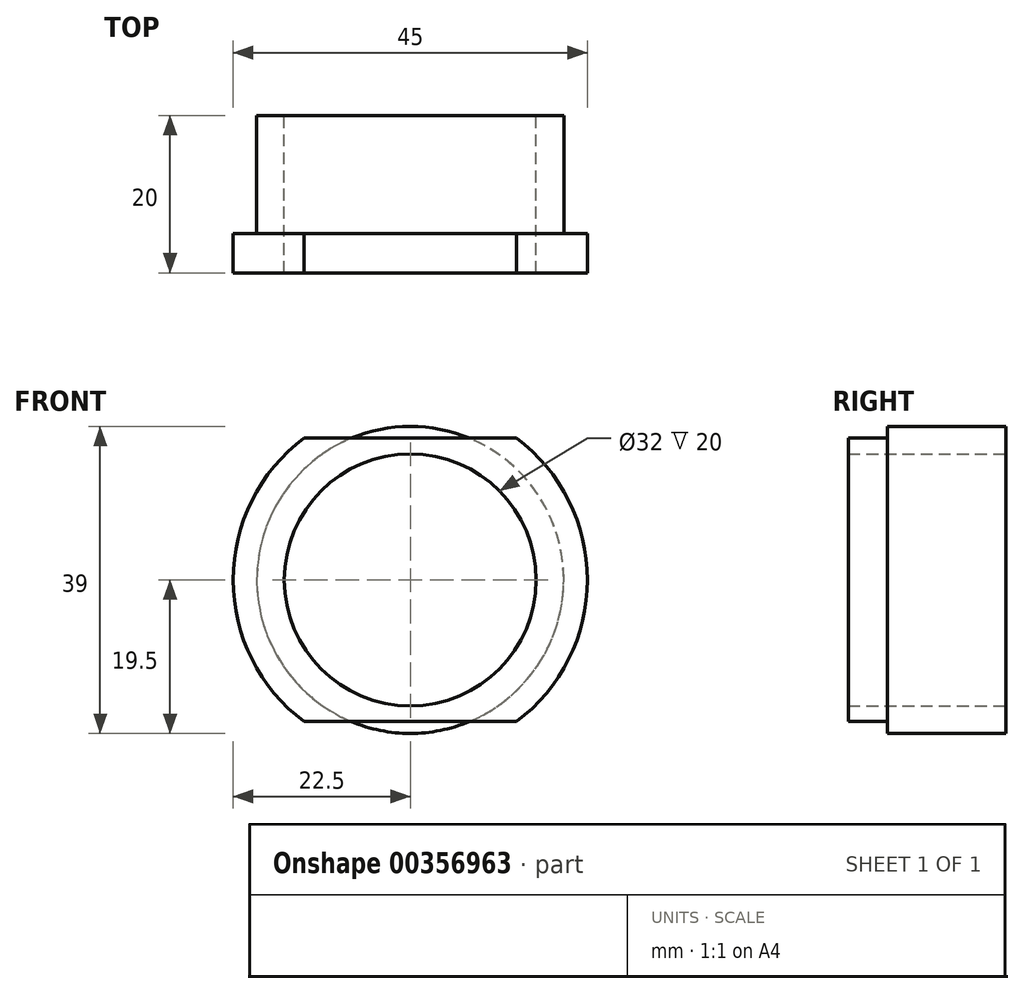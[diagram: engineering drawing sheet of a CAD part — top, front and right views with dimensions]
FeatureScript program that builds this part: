
annotation { "Feature Type Name" : "Feature", "Feature Type Description" : "" }
export const myFeature = defineFeature(function(context is Context, id is Id, definition is map)
    precondition{}
    {
        {
            var Q0;
            Q0=qCreatedBy(makeId("Front.planeOp"),FACE);
            var sketch = newSketch(context, id + "F0", { "sketchPlane" : qUnion([Q0])});
            skCircle(sketch, "E0", {"center": v(0, 0) * mm, "radius": 16 * mm});
            skLineSegment(sketch, "E1.bottom", {"start": v(13.5, 18) * mm, "end": v(-13.5, 18) * mm});
            skLineSegment(sketch, "E1.top", {"start": v(13.5, -18) * mm, "end": v(-13.5, -18) * mm});
            skArc(sketch, "E2", {"start": v(13.5, -18) * mm, "mid": v(22.5, 0) * mm, "end": v(13.5, 18) * mm});
            skArc(sketch, "E3.trimOffspring", {"start": v(-13.5, 18) * mm, "mid": v(-22.5, 0) * mm, "end": v(-13.5, -18) * mm});
            skSolve(sketch);
        }
        {
            var Q0;
            Q0=makeQuery(id+"F0.imprint","IMPRINT",FACE,{"disambiguationData":[TD([[makeQuery(id+"F0.imprint","IMPRINT",EDGE,{"derivedFrom":sQuery(id+"F0.wireOp",EDGE,"E0")}),-1.0]])]});
            extrude(context, id + "F1", {"entities" : qUnion([Q0]), "depth" : 5 * mm});
        }
        {
            var Q0;
            Q0=qCreatedBy(makeId("Front.planeOp"),FACE);
            var sketch = newSketch(context, id + "F2", { "sketchPlane" : qUnion([Q0])});
            skCircle(sketch, "E4", {"center": v(0, 0) * mm, "radius": 16 * mm});
            skCircle(sketch, "E5", {"center": v(0, 0) * mm, "radius": 19.5 * mm});
            skSolve(sketch);
        }
        {
            var Q0;
            Q0=makeQuery(id+"F2.imprint","IMPRINT",FACE,{"disambiguationData":[TD([[makeQuery(id+"F2.imprint","IMPRINT",EDGE,{"derivedFrom":sQuery(id+"F2.wireOp",EDGE,"E4")}),-1.0]])]});
            extrude(context, id + "F3", {"entities" : qUnion([Q0]), "operationType" : NewBodyOperationType.ADD, "oppositeDirection" : true, "depth" : 15 * mm});
        }
    });
